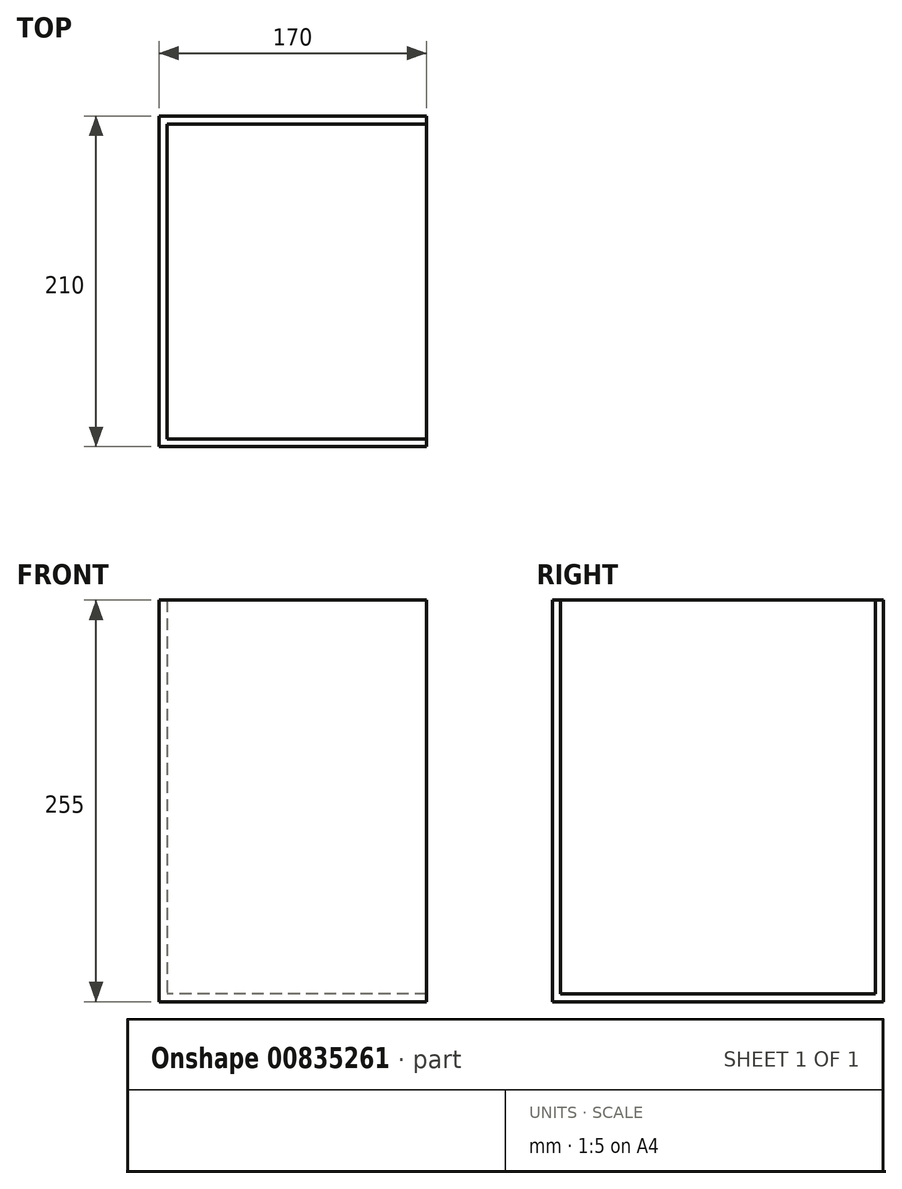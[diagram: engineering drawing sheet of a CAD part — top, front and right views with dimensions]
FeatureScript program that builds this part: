
annotation { "Feature Type Name" : "Feature", "Feature Type Description" : "" }
export const myFeature = defineFeature(function(context is Context, id is Id, definition is map)
    precondition{}
    {
        {
            var Q0;
            Q0=qCreatedBy(makeId("Top.planeOp"),FACE);
            var sketch = newSketch(context, id + "F0", { "sketchPlane" : qUnion([Q0])});
            skLineSegment(sketch, "E0.bottom", {"start": v(0, 0) * mm, "end": v(170, 0) * mm});
            skLineSegment(sketch, "E0.top", {"start": v(0, 210) * mm, "end": v(170, 210) * mm});
            skLineSegment(sketch, "E0.left", {"start": v(0, 0) * mm, "end": v(0, 210) * mm});
            skLineSegment(sketch, "E0.right", {"start": v(170, 0) * mm, "end": v(170, 210) * mm});
            skSolve(sketch);
        }
        {
            var Q0;
            Q0=makeQuery(id+"F0.imprint","IMPRINT",FACE,{"disambiguationData":[TD([[makeQuery(id+"F0.imprint","IMPRINT",EDGE,{"derivedFrom":sQuery(id+"F0.wireOp",EDGE,"E0.bottom")}),1.0]])]});
            extrude(context, id + "F1", {"entities" : qUnion([Q0]), "depth" : 5 * mm, "offsetDistance" : 25 * mm});
        }
        {
            var Q0;
            Q0=makeQuery(id+"F1.opExtrude","CAP_FACE",FACE,{"disambiguationData":[OSD([sQuery(id+"F0.wireOp",EDGE,"E0.bottom"),sQuery(id+"F0.wireOp",EDGE,"E0.top"),sQuery(id+"F0.wireOp",EDGE,"E0.left"),sQuery(id+"F0.wireOp",EDGE,"E0.right")])],"isStart":false});
            var sketch = newSketch(context, id + "F2", { "sketchPlane" : qUnion([Q0])});
            skLineSegment(sketch, "E1.bottom", {"start": v(170, 0) * mm, "end": v(0, 0) * mm});
            skLineSegment(sketch, "E1.top", {"start": v(170, 5) * mm, "end": v(0, 5) * mm});
            skLineSegment(sketch, "E1.left", {"start": v(170, 0) * mm, "end": v(170, 5) * mm});
            skLineSegment(sketch, "E1.right", {"start": v(0, 0) * mm, "end": v(0, 5) * mm});
            skLineSegment(sketch, "E2.bottom", {"start": v(170, 210) * mm, "end": v(0, 210) * mm});
            skLineSegment(sketch, "E2.top", {"start": v(170, 205) * mm, "end": v(0, 205) * mm});
            skLineSegment(sketch, "E2.left", {"start": v(170, 210) * mm, "end": v(170, 205) * mm});
            skLineSegment(sketch, "E2.right", {"start": v(0, 210) * mm, "end": v(0, 205) * mm});
            skLineSegment(sketch, "E3.bottom", {"start": v(0, 210) * mm, "end": v(5, 210) * mm});
            skLineSegment(sketch, "E3.top", {"start": v(0, 0) * mm, "end": v(5, 0) * mm});
            skLineSegment(sketch, "E3.left", {"start": v(0, 210) * mm, "end": v(0, 0) * mm});
            skLineSegment(sketch, "E3.right", {"start": v(5, 210) * mm, "end": v(5, 0) * mm});
            skSolve(sketch);
        }
        {
            var Q0;
            {var subQ0=sQuery(id+"F2.wireOp",EDGE,"E2.bottom");Q0=makeQuery(id+"F2.imprint","IMPRINT",FACE,{"disambiguationData":[TD([[makeQuery(id+"F2.imprint","IMPRINT",EDGE,{"derivedFrom":subQ0}),-1.0]])]});}
            var Q1;
            {var subQ5=sQuery(id+"F2.wireOp",EDGE,"E3.bottom");Q1=makeQuery(id+"F2.imprint","IMPRINT",FACE,{"disambiguationData":[TD([[makeQuery(id+"F2.imprint","IMPRINT",EDGE,{"derivedFrom":subQ5}),-1.0]])]});}
            var Q2;
            {var subQ0=sQuery(id+"F2.wireOp",EDGE,"E3.left");var subQ1=sQuery(id+"F2.wireOp",EDGE,"E1.top");var subQ2=makeQuery(id+"F2.imprint","INTERSECT",VERTEX,{"derivedFrom":[subQ1,subQ0]});Q2=makeQuery(id+"F2.imprint","IMPRINT",FACE,{"disambiguationData":[TD([[makeQuery(id+"F2.imprint","IMPRINT",EDGE,{"disambiguationData":[TD([[subQ2,1.0]])],"derivedFrom":subQ1}),-1.0]])]});}
            var Q3;
            {var subQ5=sQuery(id+"F2.wireOp",EDGE,"E3.top");Q3=makeQuery(id+"F2.imprint","IMPRINT",FACE,{"disambiguationData":[TD([[makeQuery(id+"F2.imprint","IMPRINT",EDGE,{"derivedFrom":subQ5}),1.0]])]});}
            var Q4;
            {var subQ0=sQuery(id+"F2.wireOp",EDGE,"E1.bottom");Q4=makeQuery(id+"F2.imprint","IMPRINT",FACE,{"disambiguationData":[TD([[makeQuery(id+"F2.imprint","IMPRINT",EDGE,{"derivedFrom":subQ0}),1.0]])]});}
            extrude(context, id + "F3", {"entities" : qUnion([Q0, Q1, Q2, Q3, Q4]), "operationType" : NewBodyOperationType.ADD, "depth" : 250 * mm, "offsetDistance" : 25 * mm});
        }
    });
